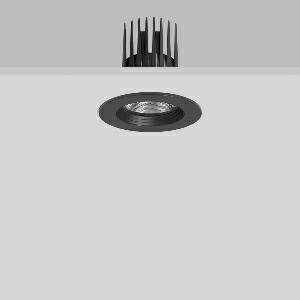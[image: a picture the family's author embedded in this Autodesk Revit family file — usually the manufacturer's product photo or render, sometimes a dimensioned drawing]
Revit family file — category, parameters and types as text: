
# Revit family: heledon_mini_e_901742_003_76_2d78
name_source: partatom
category: Lighting Fixtures
units: mm (PartAtom-declared; Revit-internal decimal feet)

## family parameters
Cut with Voids When Loaded = No
Host = Face
Light Source = No
Part Type = Normal
Room Calculation Point = No
Round Connector Dimension = Use Diameter
Shared = No

## types (1)
- HELEDON mini E (1 x LED Modul 930, 2550 lm, 3000)
    Apparent Load = 20 VA
    Approval mark = CE
    CIE Flux Codes = 95 99 100 100 100
    Color Rendering = 90
    Color Temperature = 3000
    Default Elevation = 1800 mm
    Description = Series: HELEDON mini
Round recessed downlight. Housing: die-cast aluminium, powder-coated. Black plastic ring and recessed LED to prevent glare from the side. Optical assembly with reflector made of MIRO-Silver with 98% total light reflection for outstanding efficiency - can be changed without tools. Best colour rendering index Ra>90. Suitable for Recessed ceiling mounting. Installation without tools thanks to spring fastening system. Including separate LED converter with connecting cable 600 mm.High quality converter without flickering and stroboscopic effect. Through-wiring box (5 pole) available as accessory. The following accessories can be mounted without use of tools: interchangeable lenses, decorative glasses, honeycomb louvre, clear and frosted diffusers, white interchangeable plastic ring. 
Colour: deep black, matt (RAL 9005)
Diameter: 124 mm
Height: 3 mm
Cut-out diameter: 114 mm
Recess height: 170 mm
Luminaire: recess height: 120 mm
Lamp: LED
Socket: without socket
Colour temperature: 3000K
Colour rendering index (CRI): 92
System power: 20 W
Rated luminous flux: 2550 lm
Luminous efficiency: 128 lm/W
Control gear: Converter, dimmable, DALI
Protection class: II
Type of protection: IP 20
    Height = 0 mm  [stored 0 ft]
    Lamp = 1 x LED Modul 930
    Lamp Light Flux = 2550 lm
    Lamp count = 1
    Length = 124 mm  [stored 0.406824 ft]
    Lifetime = 50000 h
    Luminous efficacy = 128 lm/W
    Manufacturer = RZB
    ModVariant = No
    Model = 901742.003.76
    Mounting Place = Ceiling
    Mounting Type = Recessed
    Number of Poles = 1
    OnlyDefault = Yes
    Power Factor = 1
    Product Name = HELEDON mini E
    Product group = Recessed downlights
    ProductGroupID = 402
    Protection Class = Protection class II
    Protection Degree = IP 20
    RLX_Detail_Level = 1
    RLX_Emergency_Light_Flux = 0 lm
    RLX_Emergency_Type = 0
    RLX_Emergency_Type_DB = No
    RlxData = <blob elided: 125797 chars, md5=7cd45ce2>
    Socket = socket
    Standby Power = 0 W
    System Light Flux = 2550 lm
    System Power = 20 W
    Type Comments = Product without accessories
    Type Image = 901657.003.jpg
    URL = http://relux.com
    VarID = ---
    Voltage = 230 V
    Voltage Range = 220-240 V
    Weight = 0.00 kg
    Width = 0 mm  [stored 0 ft]

note: [stored X ft] marks values corroborated as IEEE doubles in the binary element streams (Revit-internal decimal feet)

## geometry (parser evidence)
native form markers: Blend x4, Sweep x10
no freeform markers — native parametric forms only
